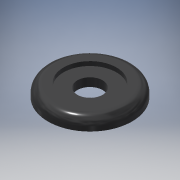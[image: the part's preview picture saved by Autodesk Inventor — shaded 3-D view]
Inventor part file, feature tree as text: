
AUTODESK INVENTOR PART (.ipt)
format: ipt  version: 2018 (Build 220112000, 112)  size: 166,912 bytes
history: native  units: mm
features: revolve x1, direct_edit x1, sketch x1, other x1
ambient origin geometry x8: Origin, YZ Plane, XZ Plane, XY Plane, X Axis, Y Axis, Z Axis, Center Point
bodies: Solid1 (feature_tree)
feature tree (4):
  revolve  "Revolution1"  [1 undecoded]
  direct_edit  "Direct Edit1"
  sketch  "Sketch1"  dims[d0=5.0mm d1=4.5mm d2=3.5mm d3=1.5mm d4=1.5mm d5=0.5mm d6=0.5mm d7=2.75mm d8=1.0mm d9=0.05mm d10=90.0deg d11=6.3mm]
  other  "Size1"
note: 1 required parameter value undecoded (feature->parameter linkage not recoverable at this tier; creation-order binding heuristic only, values carry confidence <= 0.55)
